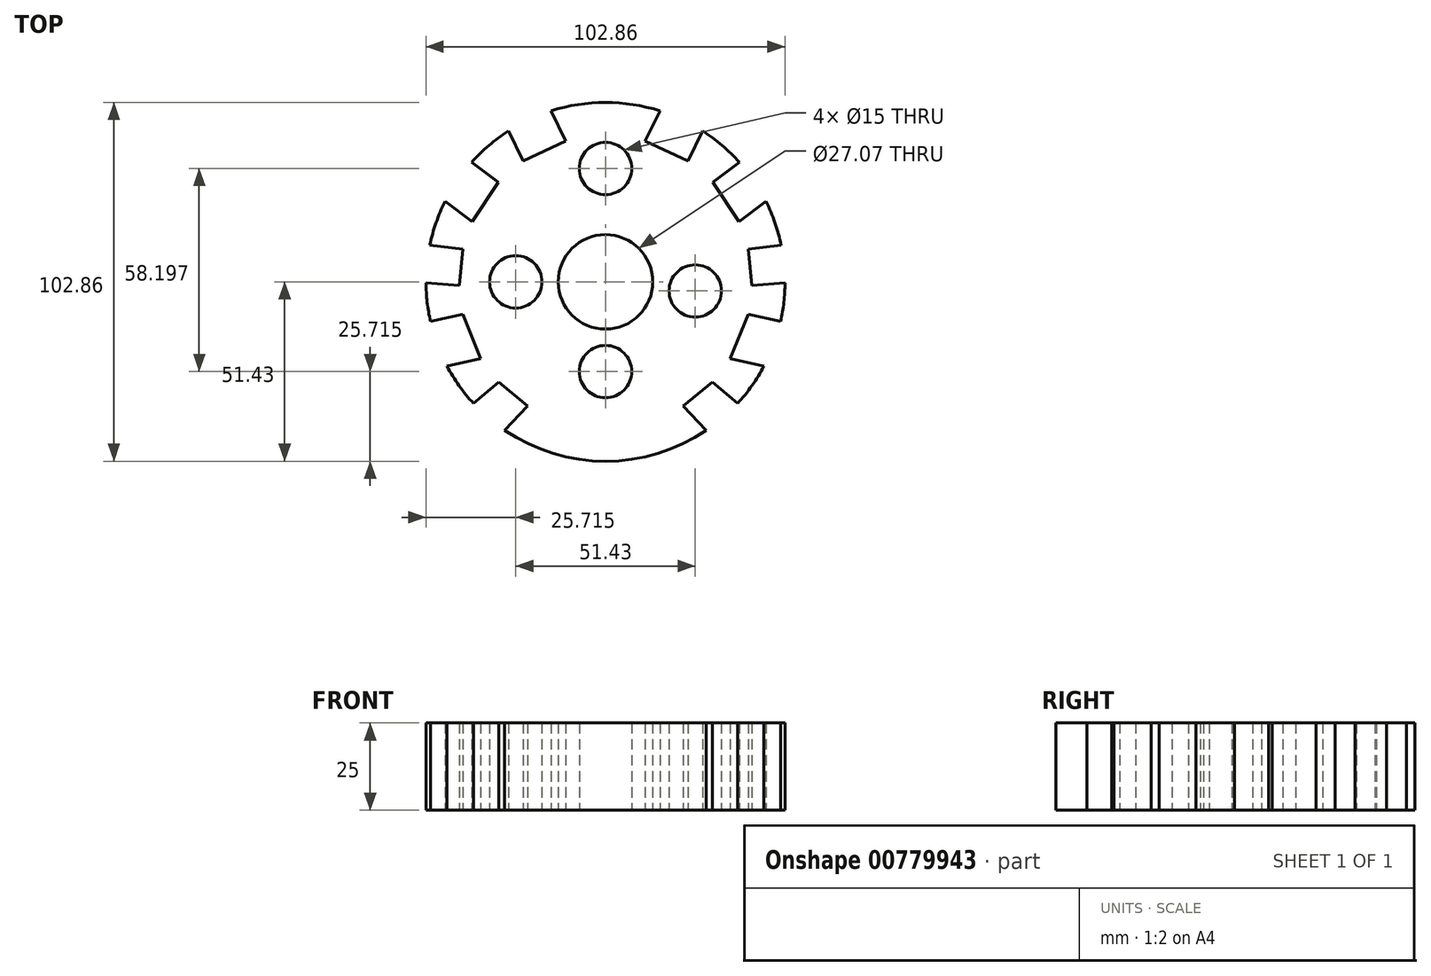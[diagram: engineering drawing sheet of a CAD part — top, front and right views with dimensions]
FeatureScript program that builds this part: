
annotation { "Feature Type Name" : "Feature", "Feature Type Description" : "" }
export const myFeature = defineFeature(function(context is Context, id is Id, definition is map)
    precondition{}
    {
        {
            var Q0;
            Q0=qCreatedBy(makeId("Top.planeOp"),FACE);
            var sketch = newSketch(context, id + "F0", { "sketchPlane" : qUnion([Q0])});
            skArc(sketch, "E0", {"start": v(0, -51.43) * mm, "mid": v(51.43, 0) * mm, "end": v(0, 51.43) * mm});
            skLineSegment(sketch, "E1", {"start": v(0, 0) * mm, "end": v(41.25, 30.72) * mm, "construction": true});
            skLineSegment(sketch, "E2", {"start": v(0, 0) * mm, "end": v(41.27, -30.7) * mm, "construction": true});
            skLineSegment(sketch, "E3", {"start": v(0, 0) * mm, "end": v(22.54, 46.23) * mm, "construction": true});
            skLineSegment(sketch, "E4", {"start": v(22.28, -46.35) * mm, "end": v(0, 0) * mm, "construction": true});
            skLineSegment(sketch, "E5", {"start": v(0, 0) * mm, "end": v(50.17, -11.33) * mm, "construction": true});
            skLineSegment(sketch, "E6", {"start": v(51.43, 0) * mm, "end": v(50.12, 11.56) * mm, "construction": true});
            skLineSegment(sketch, "E7", {"start": v(50.12, 11.56) * mm, "end": v(0, 0) * mm, "construction": true});
            skArc(sketch, "E8", {"start": v(18.17, -37.8) * mm, "mid": v(40.89, 9.32) * mm, "end": v(0, 41.94) * mm, "construction": true});
            skLineSegment(sketch, "E9", {"start": v(28.63, 30.64) * mm, "end": v(30.72, 28.54) * mm});
            skLineSegment(sketch, "E10", {"start": v(0, 0) * mm, "end": v(51.43, 0) * mm, "construction": true});
            skLineSegment(sketch, "E11", {"start": v(23.65, 34.63) * mm, "end": v(11.38, 40.36) * mm, "construction": true});
            skLineSegment(sketch, "E12", {"start": v(38.22, 17.26) * mm, "end": v(30.72, 28.54) * mm, "construction": true});
            skLineSegment(sketch, "E13", {"start": v(41.92, -1.04) * mm, "end": v(40.86, 9.42) * mm, "construction": true});
            skLineSegment(sketch, "E14", {"start": v(35.74, -21.95) * mm, "end": v(40.9, -9.24) * mm, "construction": true});
            skLineSegment(sketch, "E15", {"start": v(22.3, -35.52) * mm, "end": v(30.6, -28.67) * mm, "construction": true});
            skLineSegment(sketch, "E16", {"start": v(0, 51.43) * mm, "end": v(0, -51.43) * mm, "construction": true});
            skLineSegment(sketch, "E17", {"start": v(11.38, 40.36) * mm, "end": v(17.1, 52.08) * mm});
            skLineSegment(sketch, "E18", {"start": v(29.36, 46.35) * mm, "end": v(23.65, 34.63) * mm});
            skLineSegment(sketch, "E19", {"start": v(11.38, 40.36) * mm, "end": v(23.65, 34.63) * mm});
            skLineSegment(sketch, "E20", {"start": v(30.72, 28.54) * mm, "end": v(42, 36.95) * mm});
            skLineSegment(sketch, "E21", {"start": v(42, 36.95) * mm, "end": v(50.09, 26.1) * mm});
            skLineSegment(sketch, "E22", {"start": v(50.09, 26.1) * mm, "end": v(38.22, 17.26) * mm});
            skLineSegment(sketch, "E23", {"start": v(30.72, 28.54) * mm, "end": v(38.22, 17.26) * mm});
            skLineSegment(sketch, "E24", {"start": v(41.92, -1.04) * mm, "end": v(40.86, 9.42) * mm});
            skLineSegment(sketch, "E25", {"start": v(54.34, 10.96) * mm, "end": v(54.34, 0) * mm});
            skLineSegment(sketch, "E26", {"start": v(54.34, 0) * mm, "end": v(41.92, -1.04) * mm});
            skLineSegment(sketch, "E27", {"start": v(40.9, -9.24) * mm, "end": v(55.93, -12.63) * mm});
            skLineSegment(sketch, "E28", {"start": v(55.93, -12.63) * mm, "end": v(52.95, -25.83) * mm});
            skLineSegment(sketch, "E29", {"start": v(52.95, -25.83) * mm, "end": v(35.74, -21.95) * mm});
            skLineSegment(sketch, "E30", {"start": v(40.9, -9.24) * mm, "end": v(35.74, -21.95) * mm});
            skLineSegment(sketch, "E31", {"start": v(30.6, -28.67) * mm, "end": v(41.92, -38.39) * mm});
            skPoint(sketch, "E32.endSnap0", {"position": v(31.3, -45.12) * mm});
            skLineSegment(sketch, "E33", {"start": v(32.9, -46.84) * mm, "end": v(22.3, -35.52) * mm});
            skLineSegment(sketch, "E34", {"start": v(22.3, -35.52) * mm, "end": v(30.6, -28.67) * mm});
            skLineSegment(sketch, "E35", {"start": v(32.9, -46.84) * mm, "end": v(41.92, -38.39) * mm});
            skLineSegment(sketch, "E36", {"start": v(54.34, 10.96) * mm, "end": v(40.86, 9.42) * mm});
            skLineSegment(sketch, "E37", {"start": v(17.1, 52.08) * mm, "end": v(29.36, 46.35) * mm});
            skLineSegment(sketch, "E38.MirrorCS", {"start": v(-28.63, 30.64) * mm, "end": v(-30.72, 28.54) * mm});
            skLineSegment(sketch, "E39.MirrorCS", {"start": v(-41.92, -1.04) * mm, "end": v(-40.86, 9.42) * mm});
            skLineSegment(sketch, "E40.MirrorCS", {"start": v(-40.9, -9.24) * mm, "end": v(-35.74, -21.95) * mm});
            skLineSegment(sketch, "E41.MirrorCS", {"start": v(-22.3, -35.52) * mm, "end": v(-30.6, -28.67) * mm});
            skLineSegment(sketch, "E42.MirrorCS", {"start": v(-11.38, 40.36) * mm, "end": v(-23.65, 34.63) * mm});
            skLineSegment(sketch, "E43.MirrorCS", {"start": v(-40.9, -9.24) * mm, "end": v(-55.93, -12.63) * mm});
            skLineSegment(sketch, "E44.MirrorCS", {"start": v(-30.72, 28.54) * mm, "end": v(-38.22, 17.26) * mm});
            skLineSegment(sketch, "E45.MirrorCS", {"start": v(-41.92, -1.04) * mm, "end": v(-40.86, 9.42) * mm, "construction": true});
            skLineSegment(sketch, "E46.MirrorCS", {"start": v(-11.38, 40.36) * mm, "end": v(-17.1, 52.08) * mm});
            skLineSegment(sketch, "E47.MirrorCS", {"start": v(-50.12, 11.56) * mm, "end": v(0, 0) * mm, "construction": true});
            skLineSegment(sketch, "E48.MirrorCS", {"start": v(-42, 36.95) * mm, "end": v(-50.09, 26.1) * mm});
            skLineSegment(sketch, "E49.MirrorCS", {"start": v(-54.34, 10.96) * mm, "end": v(-40.86, 9.42) * mm});
            skLineSegment(sketch, "E50.MirrorCS", {"start": v(-30.72, 28.54) * mm, "end": v(-42, 36.95) * mm});
            skArc(sketch, "E51.MirrorCS", {"start": v(0, -51.43) * mm, "mid": v(-51.43, 0) * mm, "end": v(0, 51.43) * mm});
            skLineSegment(sketch, "E52.MirrorCS", {"start": v(-50.09, 26.1) * mm, "end": v(-38.22, 17.26) * mm});
            skLineSegment(sketch, "E53.MirrorCS", {"start": v(-52.95, -25.83) * mm, "end": v(-35.74, -21.95) * mm});
            skLineSegment(sketch, "E54.MirrorCS", {"start": v(-32.9, -46.84) * mm, "end": v(-22.3, -35.52) * mm});
            skLineSegment(sketch, "E55.MirrorCS", {"start": v(-22.3, -35.52) * mm, "end": v(-30.6, -28.67) * mm, "construction": true});
            skLineSegment(sketch, "E56.MirrorCS", {"start": v(-35.74, -21.95) * mm, "end": v(-40.9, -9.24) * mm, "construction": true});
            skLineSegment(sketch, "E57.MirrorCS", {"start": v(-30.6, -28.67) * mm, "end": v(-41.92, -38.39) * mm});
            skLineSegment(sketch, "E58.MirrorCS", {"start": v(0, 0) * mm, "end": v(-50.17, -11.33) * mm, "construction": true});
            skLineSegment(sketch, "E59.MirrorCS", {"start": v(-22.28, -46.35) * mm, "end": v(0, 0) * mm, "construction": true});
            skLineSegment(sketch, "E60.MirrorCS", {"start": v(-55.93, -12.63) * mm, "end": v(-52.95, -25.83) * mm});
            skLineSegment(sketch, "E61.MirrorCS", {"start": v(0, 0) * mm, "end": v(-41.25, 30.72) * mm, "construction": true});
            skLineSegment(sketch, "E62.MirrorCS", {"start": v(-23.65, 34.63) * mm, "end": v(-11.38, 40.36) * mm, "construction": true});
            skLineSegment(sketch, "E63.MirrorCS", {"start": v(0, 0) * mm, "end": v(-22.54, 46.23) * mm, "construction": true});
            skLineSegment(sketch, "E64.MirrorCS", {"start": v(-38.22, 17.26) * mm, "end": v(-30.72, 28.54) * mm, "construction": true});
            skArc(sketch, "E65.MirrorCS", {"start": v(-18.17, -37.8) * mm, "mid": v(-40.89, 9.32) * mm, "end": v(0, 41.94) * mm, "construction": true});
            skLineSegment(sketch, "E66.MirrorCS", {"start": v(-54.34, 0) * mm, "end": v(-41.92, -1.04) * mm});
            skLineSegment(sketch, "E67.MirrorCS", {"start": v(-32.9, -46.84) * mm, "end": v(-41.92, -38.39) * mm});
            skLineSegment(sketch, "E68.MirrorCS", {"start": v(0, 0) * mm, "end": v(-41.27, -30.7) * mm, "construction": true});
            skLineSegment(sketch, "E69.MirrorCS", {"start": v(-17.1, 52.08) * mm, "end": v(-29.36, 46.35) * mm});
            skPoint(sketch, "E70.MirrorP", {"position": v(-31.3, -45.12) * mm});
            skLineSegment(sketch, "E71.MirrorCS", {"start": v(-29.36, 46.35) * mm, "end": v(-23.65, 34.63) * mm});
            skLineSegment(sketch, "E72.MirrorCS", {"start": v(-51.43, 0) * mm, "end": v(-50.12, 11.56) * mm, "construction": true});
            skLineSegment(sketch, "E73.MirrorCS", {"start": v(0, 0) * mm, "end": v(-51.43, 0) * mm, "construction": true});
            skLineSegment(sketch, "E74.MirrorCS", {"start": v(-54.34, 10.96) * mm, "end": v(-54.34, 0) * mm});
            skCircle(sketch, "E75", {"center": v(0, 0) * mm, "radius": 13.53 * mm});
            skLineSegment(sketch, "E76", {"start": v(0, 51.43) * mm, "end": v(0, 13.53) * mm, "construction": true});
            skLineSegment(sketch, "E77", {"start": v(0, 13.53) * mm, "end": v(0, 32.48) * mm, "construction": true});
            skLineSegment(sketch, "E78", {"start": v(0, 0) * mm, "end": v(0, -51.43) * mm, "construction": true});
            skLineSegment(sketch, "E79", {"start": v(0, -51.43) * mm, "end": v(0, -25.72) * mm, "construction": true});
            skCircle(sketch, "E80", {"center": v(0, 32.48) * mm, "radius": 7.5 * mm});
            skCircle(sketch, "E81", {"center": v(0, -25.72) * mm, "radius": 7.5 * mm});
            skCircle(sketch, "E82", {"center": v(25.72, -2.61) * mm, "radius": 7.5 * mm});
            skPoint(sketch, "E82.centerSnap0", {"position": v(25.72, 0) * mm});
            skCircle(sketch, "E83", {"center": v(-25.72, 0) * mm, "radius": 7.5 * mm});
            skSolve(sketch);
        }
        {
            var Q0;
            {var subQ29=sQuery(id+"F0.wireOp",EDGE,"E19");Q0=makeQuery(id+"F0.imprint","IMPRINT",FACE,{"disambiguationData":[TD([[makeQuery(id+"F0.imprint","IMPRINT",EDGE,{"derivedFrom":subQ29}),-1.0]])]});}
            extrude(context, id + "F1", {"entities" : qUnion([Q0]), "depth" : 25 * mm, "offsetDistance" : 25 * mm});
        }
        {
            var Q0;
            Q0=makeQuery(id+"F0.imprint","IMPRINT",FACE,{"disambiguationData":[TD([[makeQuery(id+"F0.imprint","IMPRINT",EDGE,{"derivedFrom":sQuery(id+"F0.wireOp",EDGE,"E75")}),1.0]])]});
            extrude(context, id + "F2", {"entities" : qUnion([Q0]), "operationType" : NewBodyOperationType.REMOVE, "oppositeDirection" : true, "depth" : 0.4 * mm, "offsetDistance" : 25 * mm});
        }
        {
            var Q0;
            Q0=makeQuery(id+"F0.imprint","IMPRINT",FACE,{"disambiguationData":[TD([[makeQuery(id+"F0.imprint","IMPRINT",EDGE,{"derivedFrom":sQuery(id+"F0.wireOp",EDGE,"E80")}),1.0]])]});
            var Q1;
            Q1=makeQuery(id+"F0.imprint","IMPRINT",FACE,{"disambiguationData":[TD([[makeQuery(id+"F0.imprint","IMPRINT",EDGE,{"derivedFrom":sQuery(id+"F0.wireOp",EDGE,"E83")}),1.0]])]});
            var Q2;
            Q2=makeQuery(id+"F0.imprint","IMPRINT",FACE,{"disambiguationData":[TD([[makeQuery(id+"F0.imprint","IMPRINT",EDGE,{"derivedFrom":sQuery(id+"F0.wireOp",EDGE,"E82")}),1.0]])]});
            var Q3;
            Q3=makeQuery(id+"F0.imprint","IMPRINT",FACE,{"disambiguationData":[TD([[makeQuery(id+"F0.imprint","IMPRINT",EDGE,{"derivedFrom":sQuery(id+"F0.wireOp",EDGE,"E81")}),1.0]])]});
            extrude(context, id + "F3", {"entities" : qUnion([Q0, Q1, Q2, Q3]), "operationType" : NewBodyOperationType.REMOVE, "oppositeDirection" : true, "depth" : 25 * mm, "offsetDistance" : 25 * mm});
        }
    });
